# Revit family: 1215xxx - Astro FUSE 3 (CE)
name_source: partatom
category: Lighting Fixtures
units: mm (PartAtom-declared; Revit-internal decimal feet)

## family parameters
Always vertical = Yes
Cut with Voids When Loaded = No
Host = Wall
Light Source = Yes
OmniClass Number = 23.80.70.00
OmniClass Title = Lighting
Part Type = Normal
Room Calculation Point = No
Round Connector Dimension = Use Diameter
Shared = No

## types (6) — shared parameters
ADA compliant = N / A
Color Filter = 16777215
Dimmable = No
Dimming Lamp Color Temperature Shift = <None>
Driver Included = Yes
Driver Required = No
Efficacy (lm/w) = 39
Electrical Class = 1
Emit from Line Length = 610 mm
Lamp = LED
Light Source Fixed = Yes
Location / IP Rating = IP20
Main Material = Metal - Aluminium / Polycarbonate
Manufacturer = Astro Lighting Ltd
Manufacturer URL - Europe and Rest of World = www.astrolighting.com
Manufacturer URL - North America = us.astrolighting.com
Photometric Web File = 1215081_Fuse LED USB Matt White_Photometry_IES_Iss. 01.ies
Power (Watts) = 3.6
Product CCT = 2700K
Product CRI = 90
Product Dimensions (MM) = 200 x 75 x 92
Product Location = Wall / Headboard
Product Name = Fuse 3 LED
Product URL = https://www.astrolighting.com
Tilt Angle = 60.00°
URL = www.astrolighting.com
zero-valued in all types: Default Elevation

## per-type parameters (varying)
| type | Main Finish | Product SKU | Product Weight (KG) |
| Astro Fuse 3 LED - Matt White | Matt White | 1215122 | 0.5 |
| Astro Fuse 3 LED - Matt Black | Matt Black | 1215123 | 0.5 |
| Astro Fuse 3 LED - Polished Chrome | Polished Chrome | 1215124 | 0.51 |
| Astro Fuse 3 LED - Matt Nickel | Matt Nickel | 1215125 | 0.5 |
| Astro Fuse 3 LED - Bronze | Bronze | 1215126 | 0.5 |
| Astro Fuse 3 LED - Matt Gold | Matt Gold | 1215127 | 0.5 |

## geometry (parser evidence)
native form markers: Sweep x3
no freeform markers — native parametric forms only
